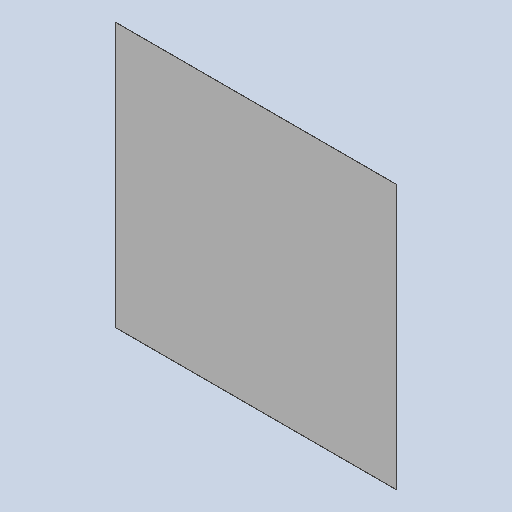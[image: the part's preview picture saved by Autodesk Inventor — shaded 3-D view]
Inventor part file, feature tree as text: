
AUTODESK INVENTOR PART (.ipt)
format: ipt  version: 2024.3 (Build 283343000, 343)  size: 101,376 bytes
history: native  units: in
note: dims shown in document units (in); Inventor stores cm internally (conversion verified against a paired STEP export)
features: extrude x1, sketch x1
ambient origin geometry x8: Origin, YZ Plane, XZ Plane, XY Plane, X Axis, Y Axis, Z Axis, Center Point
bodies: Solid1 (feature_tree)
feature tree (2):
  extrude  "Extrusion1"  [1 undecoded]
  sketch  "Sketch1"  dims[d0=0.001in d1=0.0in]
note: 1 required parameter value undecoded (feature->parameter linkage not recoverable at this tier; creation-order binding heuristic only, values carry confidence <= 0.55)
